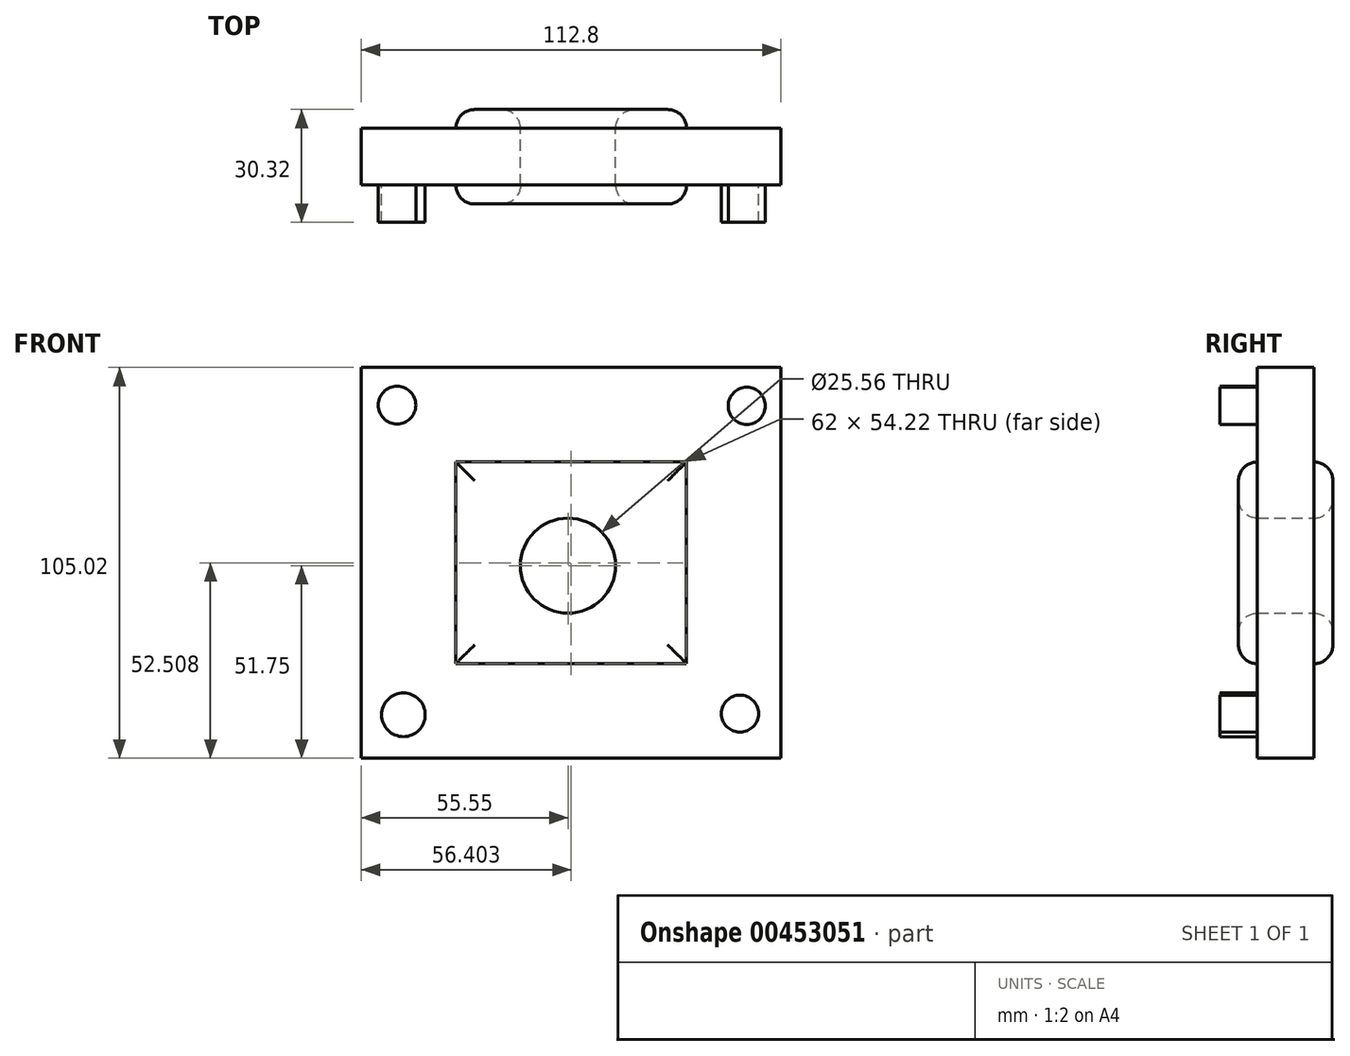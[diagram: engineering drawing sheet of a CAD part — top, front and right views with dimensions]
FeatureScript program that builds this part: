
annotation { "Feature Type Name" : "Feature", "Feature Type Description" : "" }
export const myFeature = defineFeature(function(context is Context, id is Id, definition is map)
    precondition{}
    {
        {
            var Q0;
            Q0=qCreatedBy(makeId("Front.planeOp"),FACE);
            var sketch = newSketch(context, id + "F0", { "sketchPlane" : qUnion([Q0])});
            skLineSegment(sketch, "E0.bottom", {"start": v(-30.15, 27.87) * mm, "end": v(31.85, 27.87) * mm});
            skLineSegment(sketch, "E0.top", {"start": v(-30.15, -26.35) * mm, "end": v(31.85, -26.35) * mm});
            skLineSegment(sketch, "E0.left", {"start": v(-30.15, 27.87) * mm, "end": v(-30.15, -26.35) * mm});
            skLineSegment(sketch, "E0.right", {"start": v(31.85, 27.87) * mm, "end": v(31.85, -26.35) * mm});
            skCircle(sketch, "E1", {"center": v(0, 0) * mm, "radius": 12.78 * mm});
            skSolve(sketch);
        }
        {
            var Q0;
            Q0 = qSketchRegion(id + "F0", true);
            extrude(context, id + "F1", {"entities" : qUnion([Q0]), "depth" : 25.4 * mm});
        }
        {
            var Q0;
            Q0=makeQuery(id+"F1.opExtrude","CAP_EDGE",EDGE,{"disambiguationData":[OSD([sQuery(id+"F0.wireOp",EDGE,"E0.bottom")])],"isStart":false});
            var Q1;
            Q1=makeQuery(id+"F1.opExtrude","CAP_FACE",FACE,{"disambiguationData":[OSD([sQuery(id+"F0.wireOp",EDGE,"E0.bottom"),sQuery(id+"F0.wireOp",EDGE,"E0.top"),sQuery(id+"F0.wireOp",EDGE,"E0.left"),sQuery(id+"F0.wireOp",EDGE,"E0.right"),sQuery(id+"F0.wireOp",EDGE,"E1")])],"isStart":false});
            var Q2;
            Q2=makeQuery(id+"F1.opExtrude","CAP_EDGE",EDGE,{"disambiguationData":[OSD([sQuery(id+"F0.wireOp",EDGE,"E0.bottom")])],"isStart":true});
            var Q3;
            Q3=makeQuery(id+"F1.opExtrude","CAP_FACE",FACE,{"disambiguationData":[OSD([sQuery(id+"F0.wireOp",EDGE,"E0.bottom"),sQuery(id+"F0.wireOp",EDGE,"E0.top"),sQuery(id+"F0.wireOp",EDGE,"E0.left"),sQuery(id+"F0.wireOp",EDGE,"E0.right"),sQuery(id+"F0.wireOp",EDGE,"E1")])],"isStart":true});
            fillet(context, id + "F2", {"entities" : qUnion([Q0, Q1, Q2, Q3]), "radius" : 5.08 * mm, "tangentPropagation" : true, "allowEdgeOverflow" : false});
        }
        {
            var Q0;
            Q0=makeQuery(id+"F1.opExtrude","SWEPT_FACE",FACE,{"disambiguationData":[OSD([sQuery(id+"F0.wireOp",EDGE,"E0.bottom")])]});
            extrude(context, id + "F3", {"entities" : qUnion([Q0]), "operationType" : NewBodyOperationType.ADD, "depth" : 25.4 * mm});
        }
        {
            var Q0;
            Q0=makeQuery(id+"F1.opExtrude","SWEPT_FACE",FACE,{"disambiguationData":[OSD([sQuery(id+"F0.wireOp",EDGE,"E0.top")])]});
            extrude(context, id + "F4", {"entities" : qUnion([Q0]), "operationType" : NewBodyOperationType.ADD, "depth" : 25.4 * mm});
        }
        {
            var Q0;
            {var subQ0=sQuery(id+"F0.wireOp",EDGE,"E0.left");Q0=makeQuery(id+"F4.boolean.opBoolean","MERGE",FACE,{"derivedFrom":[makeQuery(id+"F3.boolean.opBoolean","MERGE",FACE,{"derivedFrom":[makeQuery(id+"F1.opExtrude","SWEPT_FACE",FACE,{"disambiguationData":[OSD([subQ0])]}),makeQuery(id+"F3.opExtrude","SWEPT_FACE",FACE,{"disambiguationData":[OSD([sQuery(id+"F0.wireOp",EDGE,"E0.bottom"),subQ0])]})]}),makeQuery(id+"F4.opExtrude","SWEPT_FACE",FACE,{"disambiguationData":[OSD([sQuery(id+"F0.wireOp",EDGE,"E0.top"),subQ0])]})]});}
            extrude(context, id + "F5", {"entities" : qUnion([Q0]), "operationType" : NewBodyOperationType.ADD, "depth" : 25.4 * mm});
        }
        {
            var Q0;
            {var subQ0=sQuery(id+"F0.wireOp",EDGE,"E0.right");Q0=makeQuery(id+"F4.boolean.opBoolean","MERGE",FACE,{"derivedFrom":[makeQuery(id+"F3.boolean.opBoolean","MERGE",FACE,{"derivedFrom":[makeQuery(id+"F1.opExtrude","SWEPT_FACE",FACE,{"disambiguationData":[OSD([subQ0])]}),makeQuery(id+"F3.opExtrude","SWEPT_FACE",FACE,{"disambiguationData":[OSD([sQuery(id+"F0.wireOp",EDGE,"E0.bottom"),subQ0])]})]}),makeQuery(id+"F4.opExtrude","SWEPT_FACE",FACE,{"disambiguationData":[OSD([sQuery(id+"F0.wireOp",EDGE,"E0.top"),subQ0])]})]});}
            extrude(context, id + "F6", {"entities" : qUnion([Q0]), "operationType" : NewBodyOperationType.ADD, "depth" : 25.4 * mm});
        }
        {
            var Q0;
            {var subQ0=sQuery(id+"F0.wireOp",EDGE,"E0.right");var subQ1=makeQuery(id+"F1.opExtrude","SWEPT_FACE",FACE,{"disambiguationData":[OSD([subQ0])]});var subQ2=sQuery(id+"F0.wireOp",EDGE,"E0.top");var subQ3=makeQuery(id+"F1.opExtrude","SWEPT_FACE",FACE,{"disambiguationData":[OSD([subQ2])]});var subQ4=makeQuery(id+"F1.opExtrude","CAP_EDGE",EDGE,{"disambiguationData":[OSD([subQ0])],"isStart":false});var subQ5=makeQuery(id+"F1.opExtrude","CAP_EDGE",EDGE,{"disambiguationData":[OSD([subQ2])],"isStart":false});var subQ6=sQuery(id+"F0.wireOp",EDGE,"E0.bottom");var subQ7=makeQuery(id+"F1.opExtrude","SWEPT_FACE",FACE,{"disambiguationData":[OSD([subQ6])]});var subQ8=makeQuery(id+"F1.opExtrude","CAP_EDGE",EDGE,{"disambiguationData":[OSD([subQ6])],"isStart":false});var subQ9=sQuery(id+"F0.wireOp",EDGE,"E0.left");var subQ10=makeQuery(id+"F1.opExtrude","SWEPT_FACE",FACE,{"disambiguationData":[OSD([subQ9])]});var subQ11=makeQuery(id+"F1.opExtrude","CAP_EDGE",EDGE,{"disambiguationData":[OSD([subQ9])],"isStart":false});Q0=makeQuery(id+"F6.boolean.opBoolean","MERGE",FACE,{"derivedFrom":[makeQuery(id+"F5.boolean.opBoolean","MERGE",FACE,{"derivedFrom":[makeQuery(id+"F3.opExtrude","SWEPT_FACE",FACE,{"disambiguationData":[OSD([subQ6]),TDD([makeQuery(id+"F2.opFillet","BLEND_EDGE",EDGE,{"blendedFrom":[subQ8,subQ7],"blendedInto":[subQ7]})])]}),makeQuery(id+"F4.opExtrude","SWEPT_FACE",FACE,{"disambiguationData":[OSD([subQ2]),TDD([makeQuery(id+"F2.opFillet","BLEND_EDGE",EDGE,{"blendedFrom":[subQ5,subQ3],"blendedInto":[subQ3]})])]}),makeQuery(id+"F5.opExtrude","SWEPT_FACE",FACE,{"disambiguationData":[OSD([subQ6,subQ2,subQ9]),TDD([makeQuery(id+"F2.opFillet","BLEND_EDGE",EDGE,{"blendedFrom":[subQ11,subQ10],"blendedInto":[subQ10]}),makeQuery(id+"F3.opExtrude","SWEPT_EDGE",EDGE,{"disambiguationData":[OSD([subQ6,subQ9]),TDD([makeQuery(id+"F2.opFillet","BLEND_VERTEX",VERTEX,{"blendedFrom":[subQ8,subQ11,subQ7,subQ10],"blendedInto":[subQ7,subQ10]})])]}),makeQuery(id+"F4.opExtrude","SWEPT_EDGE",EDGE,{"disambiguationData":[OSD([subQ2,subQ9]),TDD([makeQuery(id+"F2.opFillet","BLEND_VERTEX",VERTEX,{"blendedFrom":[subQ5,subQ11,subQ3,subQ10],"blendedInto":[subQ3,subQ10]})])]})])]})]}),makeQuery(id+"F6.opExtrude","SWEPT_FACE",FACE,{"disambiguationData":[OSD([subQ6,subQ2,subQ0]),TDD([makeQuery(id+"F2.opFillet","BLEND_EDGE",EDGE,{"blendedFrom":[subQ4,subQ1],"blendedInto":[subQ1]}),makeQuery(id+"F3.opExtrude","SWEPT_EDGE",EDGE,{"disambiguationData":[OSD([subQ6,subQ0]),TDD([makeQuery(id+"F2.opFillet","BLEND_VERTEX",VERTEX,{"blendedFrom":[subQ8,subQ4,subQ7,subQ1],"blendedInto":[subQ7,subQ1]})])]}),makeQuery(id+"F4.opExtrude","SWEPT_EDGE",EDGE,{"disambiguationData":[OSD([subQ2,subQ0]),TDD([makeQuery(id+"F2.opFillet","BLEND_VERTEX",VERTEX,{"blendedFrom":[subQ5,subQ4,subQ3,subQ1],"blendedInto":[subQ3,subQ1]})])]})])]})]});}
            var sketch = newSketch(context, id + "F7", { "sketchPlane" : qUnion([Q0])});
            skCircle(sketch, "E2", {"center": v(-45.95, 43.14) * mm, "radius": 5.06 * mm});
            skCircle(sketch, "E3", {"center": v(48.04, 42.94) * mm, "radius": 4.99 * mm});
            skCircle(sketch, "E4", {"center": v(46.22, -39.78) * mm, "radius": 4.98 * mm});
            skCircle(sketch, "E5", {"center": v(-44.24, -40.09) * mm, "radius": 5.87 * mm});
            skSolve(sketch);
        }
        {
            var Q0;
            Q0 = qSketchRegion(id + "F7", true);
            extrude(context, id + "F8", {"entities" : qUnion([Q0]), "operationType" : NewBodyOperationType.ADD, "depth" : 10 * mm});
        }
    });
